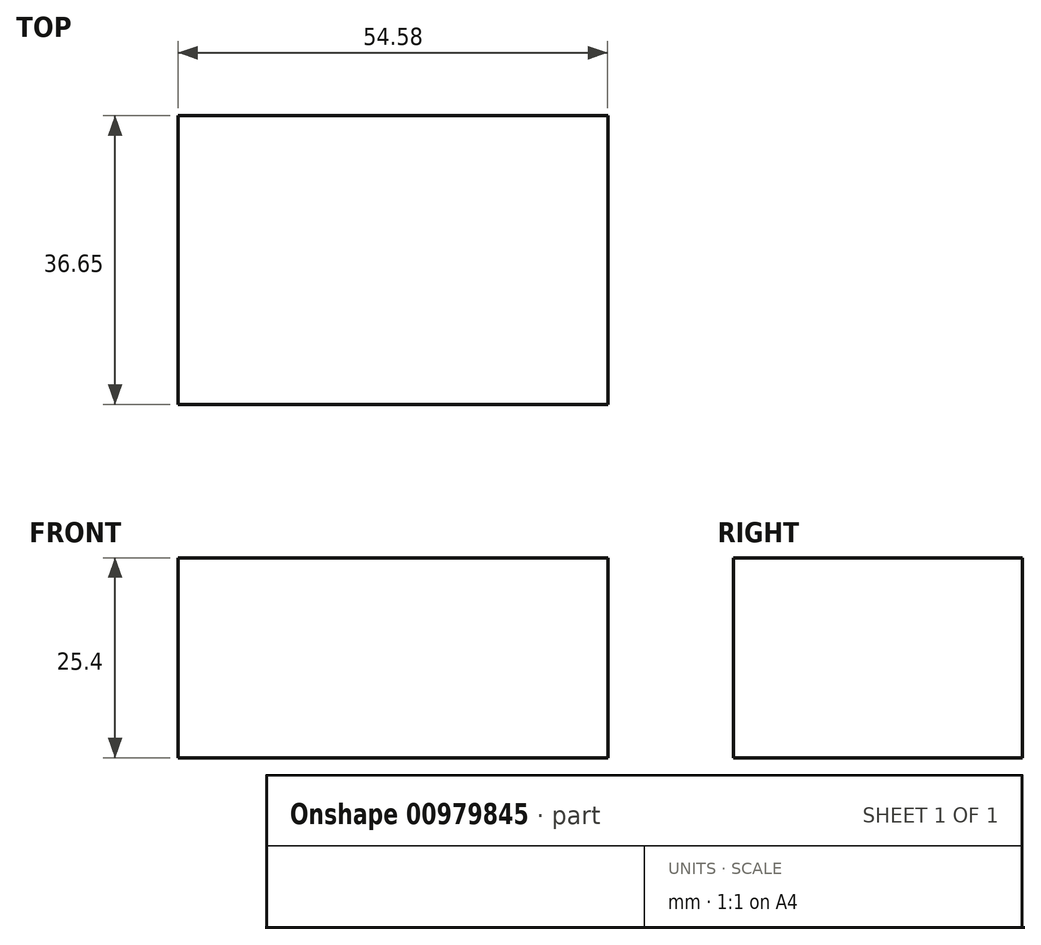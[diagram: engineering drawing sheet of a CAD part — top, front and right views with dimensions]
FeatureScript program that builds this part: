
annotation { "Feature Type Name" : "Feature", "Feature Type Description" : "" }
export const myFeature = defineFeature(function(context is Context, id is Id, definition is map)
    precondition{}
    {
        {
            var Q0;
            Q0=qCreatedBy(makeId("Top.planeOp"),FACE);
            var sketch = newSketch(context, id + "F0", { "sketchPlane" : qUnion([Q0])});
            skLineSegment(sketch, "E0.bottom", {"start": v(0, 0) * mm, "end": v(54.58, 0) * mm});
            skLineSegment(sketch, "E0.top", {"start": v(0, 36.65) * mm, "end": v(54.58, 36.65) * mm});
            skLineSegment(sketch, "E0.left", {"start": v(0, 0) * mm, "end": v(0, 36.65) * mm});
            skLineSegment(sketch, "E0.right", {"start": v(54.58, 0) * mm, "end": v(54.58, 36.65) * mm});
            skSolve(sketch);
        }
        {
            var Q0;
            Q0 = qSketchRegion(id + "F0", true);
            extrude(context, id + "F1", {"entities" : qUnion([Q0]), "oppositeDirection" : true, "depth" : 25.4 * mm, "offsetDistance" : 25.4 * mm});
        }
    });
